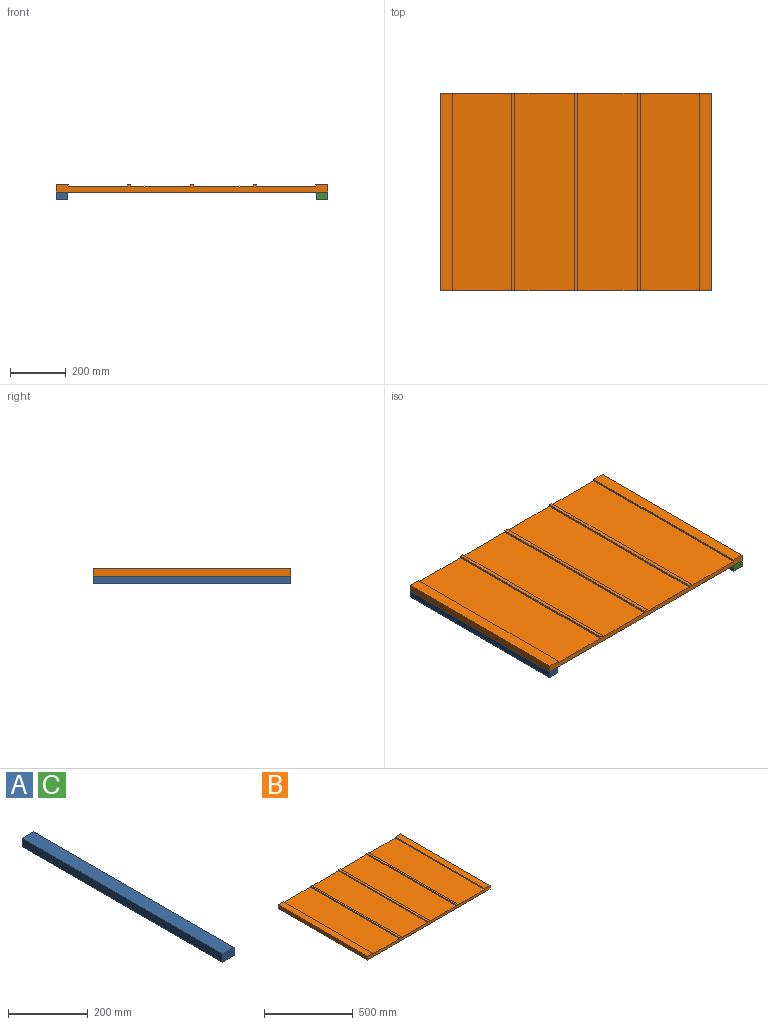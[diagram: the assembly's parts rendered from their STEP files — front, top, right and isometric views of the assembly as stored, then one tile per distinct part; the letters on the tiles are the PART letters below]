
ASSEMBLY  parts=3 mates=1
PART A: 6 faces, bbox 41.3x711.2x25.4 mm
  f0: plane 41.28x25.4mm, normal (0,1,0), area 1048.4mm2, adj f1,f3,f4,f5
  f1: plane 711.2x25.4mm, normal (-1,0,0), area 18064.5mm2, adj f0,f2,f4,f5
  f2: plane 41.28x25.4mm, normal (0,-1,0), area 1048.4mm2, adj f1,f3,f4,f5
  f3: plane 711.2x25.4mm, normal (1,0,0), area 18064.5mm2, adj f0,f2,f4,f5
  f4: plane 711.2x41.28mm, normal (0,0,1), area 29354.8mm2, adj f0,f1,f2,f3
  f5: plane 711.2x41.28mm, normal (0,0,-1), area 29354.8mm2, adj f0,f1,f2,f3
PART B: 22 faces, bbox 977.9x711.2x25.4 mm
  f0: plane 711.2x12.7mm, normal (0,0,1), area 9032.2mm2, adj f4,f5,f16,f21
  f1: plane 711.2x12.7mm, normal (0,0,1), area 9032.2mm2, adj f4,f5,f13,f18
  f2: plane 711.2x12.7mm, normal (0,0,1), area 9032.2mm2, adj f4,f5,f10,f15
  f3: plane 711.2x43.18mm, normal (0,0,1), area 30709.6mm2, adj f4,f5,f7,f12
  f4: plane 977.9x25.4mm, normal (0,-1,0), area 19419.3mm2, adj f0,f1,f2,f3,f6,f7,f8,f9
  f5: plane 977.9x25.4mm, normal (0,1,0), area 19419.3mm2, adj f0,f1,f2,f3,f6,f7,f8,f9
  f6: plane 711.2x25.4mm, normal (-1,0,0), area 18064.5mm2, adj f4,f5,f8,f9
  f7: plane 711.2x25.4mm, normal (1,0,0), area 18064.5mm2, adj f3,f4,f5,f9
  f8: plane 711.2x43.18mm, normal (0,0,1), area 30709.6mm2, adj f4,f5,f6,f19
  f9: plane 977.9x711.2mm, normal (0,0,-1), area 695482.5mm2, adj f4,f5,f6,f7
  f10: plane 711.2x6.35mm, normal (1,0,0), area 4516.1mm2, adj f2,f4,f5,f11
  f11: plane 711.2x213.36mm, normal (0,0,1), area 151741.6mm2, adj f4,f5,f10,f12
  f12: plane 711.2x6.35mm, normal (-1,0,0), area 4516.1mm2, adj f3,f4,f5,f11
  f13: plane 711.2x6.35mm, normal (1,0,0), area 4516.1mm2, adj f1,f4,f5,f14
  f14: plane 711.2x213.36mm, normal (0,0,1), area 151741.6mm2, adj f4,f5,f13,f15
  f15: plane 711.2x6.35mm, normal (-1,0,0), area 4516.1mm2, adj f2,f4,f5,f14
  f16: plane 711.2x6.35mm, normal (1,0,0), area 4516.1mm2, adj f0,f4,f5,f17
  f17: plane 711.2x213.36mm, normal (0,0,1), area 151741.6mm2, adj f4,f5,f16,f18
  f18: plane 711.2x6.35mm, normal (-1,0,0), area 4516.1mm2, adj f1,f4,f5,f17
  f19: plane 711.2x6.35mm, normal (1,0,0), area 4516.1mm2, adj f4,f5,f8,f20
  f20: plane 711.2x213.36mm, normal (0,0,1), area 151741.6mm2, adj f4,f5,f19,f21
  f21: plane 711.2x6.35mm, normal (-1,0,0), area 4516.1mm2, adj f0,f4,f5,f20
PART C: same geometry as A
PLACE A t=(-468.31,0,-12.7)mm
PLACE B at identity
PLACE C t=(468.31,0,-12.7)mm
MATE fastened A.f4 <-> B.f9  axis (0,0,1) through (-488.95,0,0)mm
